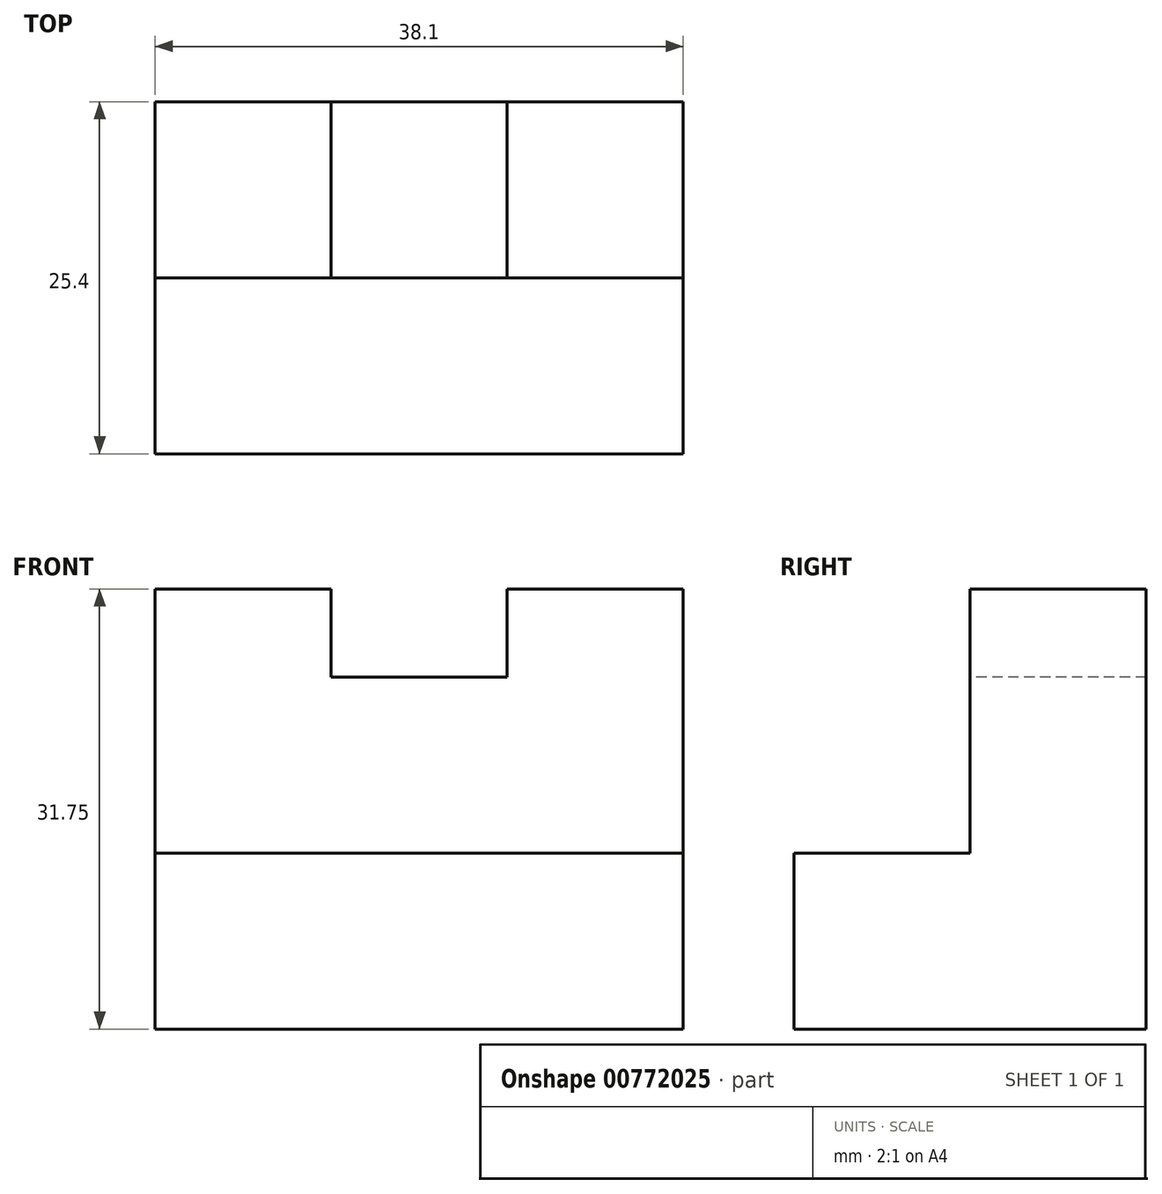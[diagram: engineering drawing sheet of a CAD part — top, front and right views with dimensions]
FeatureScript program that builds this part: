
annotation { "Feature Type Name" : "Feature", "Feature Type Description" : "" }
export const myFeature = defineFeature(function(context is Context, id is Id, definition is map)
    precondition{}
    {
        {
            var Q0;
            Q0=qCreatedBy(makeId("Right.planeOp"),FACE);
            var sketch = newSketch(context, id + "F0", { "sketchPlane" : qUnion([Q0])});
            skLineSegment(sketch, "E0", {"start": v(0, 0) * mm, "end": v(25.4, 0) * mm});
            skLineSegment(sketch, "E1", {"start": v(25.4, 0) * mm, "end": v(25.4, 31.75) * mm});
            skLineSegment(sketch, "E2", {"start": v(25.4, 31.75) * mm, "end": v(0, 31.75) * mm});
            skLineSegment(sketch, "E3", {"start": v(0, 31.75) * mm, "end": v(0, 0) * mm});
            skSolve(sketch);
        }
        {
            var Q0;
            Q0=makeQuery(id+"F0.imprint","IMPRINT",FACE,{"disambiguationData":[TD([[makeQuery(id+"F0.imprint","IMPRINT",EDGE,{"derivedFrom":sQuery(id+"F0.wireOp",EDGE,"E0")}),1.0]])]});
            extrude(context, id + "F1", {"entities" : qUnion([Q0]), "depth" : 38.1 * mm, "offsetDistance" : 25.4 * mm});
        }
        {
            var Q0;
            Q0=makeQuery(id+"F1.opExtrude","CAP_FACE",FACE,{"disambiguationData":[OSD([sQuery(id+"F0.wireOp",EDGE,"E0"),sQuery(id+"F0.wireOp",EDGE,"E1"),sQuery(id+"F0.wireOp",EDGE,"E2"),sQuery(id+"F0.wireOp",EDGE,"E3")])],"isStart":false});
            var sketch = newSketch(context, id + "F2", { "sketchPlane" : qUnion([Q0])});
            skLineSegment(sketch, "E4", {"start": v(25.4, 31.75) * mm, "end": v(12.7, 31.75) * mm});
            skLineSegment(sketch, "E5", {"start": v(12.7, 31.75) * mm, "end": v(12.7, 12.7) * mm});
            skLineSegment(sketch, "E6", {"start": v(12.7, 12.7) * mm, "end": v(0, 12.7) * mm});
            skSolve(sketch);
        }
        {
            var Q0;
            {var subQ0=sQuery(id+"F2.wireOp",EDGE,"E5");Q0=makeQuery(id+"F2.imprint","IMPRINT",FACE,{"disambiguationData":[TD([[makeQuery(id+"F2.imprint","IMPRINT",EDGE,{"derivedFrom":subQ0}),-1.0]])]});}
            extrude(context, id + "F3", {"entities" : qUnion([Q0]), "operationType" : NewBodyOperationType.REMOVE, "oppositeDirection" : true, "depth" : 38.1 * mm, "offsetDistance" : 25.4 * mm});
        }
        {
            var Q0;
            Q0=makeQuery(id+"F3.boolean.opBoolean","COPY",FACE,{"derivedFrom":makeQuery(id+"F3.opExtrude","SWEPT_FACE",FACE,{"disambiguationData":[OSD([sQuery(id+"F2.wireOp",EDGE,"E5")])]})});
            var sketch = newSketch(context, id + "F4", { "sketchPlane" : qUnion([Q0])});
            skLineSegment(sketch, "E7", {"start": v(0, 31.75) * mm, "end": v(12.7, 31.75) * mm});
            skLineSegment(sketch, "E8", {"start": v(12.7, 31.75) * mm, "end": v(12.7, 25.4) * mm});
            skLineSegment(sketch, "E9", {"start": v(12.7, 25.4) * mm, "end": v(25.4, 25.4) * mm});
            skLineSegment(sketch, "E10", {"start": v(25.4, 25.4) * mm, "end": v(25.4, 31.75) * mm});
            skLineSegment(sketch, "E11", {"start": v(25.4, 31.75) * mm, "end": v(38.1, 31.75) * mm});
            skSolve(sketch);
        }
        {
            var Q0;
            {var subQ0=sQuery(id+"F4.wireOp",EDGE,"E8");Q0=makeQuery(id+"F4.imprint","IMPRINT",FACE,{"disambiguationData":[TD([[makeQuery(id+"F4.imprint","IMPRINT",EDGE,{"derivedFrom":subQ0}),1.0]])]});}
            extrude(context, id + "F5", {"entities" : qUnion([Q0]), "operationType" : NewBodyOperationType.REMOVE, "oppositeDirection" : true, "depth" : 12.7 * mm, "offsetDistance" : 25.4 * mm});
        }
    });
